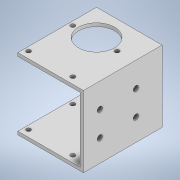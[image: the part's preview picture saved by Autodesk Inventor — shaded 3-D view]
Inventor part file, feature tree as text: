
AUTODESK INVENTOR PART (.ipt)
format: ipt  version: 2022 (Build 260153000, 153)  size: 162,816 bytes
history: native  units: mm
features: sketch x6, hole x4, extrude x2, other x1
ambient origin geometry x8: Origin, YZ Plane, XZ Plane, XY Plane, X Axis, Y Axis, Z Axis, Center Point
bodies: Body1 (feature_tree)
feature tree (13):
  other  "ソリッド1"
  extrude  "押し出し1"  Depth=48.0mm
  extrude  "押し出し2"  Depth=40.0mm
  hole  "穴1"  [1 undecoded]
  hole  "穴2"  [1 undecoded]
  hole  "穴3"  [1 undecoded]
  hole  "穴4"  [1 undecoded]
  sketch  "スケッチ1"
  sketch  "スケッチ2"
  sketch  "スケッチ3"
  sketch  "スケッチ4"
  sketch  "スケッチ5"
  sketch  "スケッチ6"
note: 4 required parameter values undecoded (feature->parameter linkage not recoverable at this tier; creation-order binding heuristic only, values carry confidence <= 0.55)
